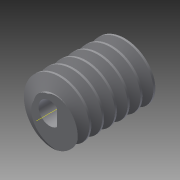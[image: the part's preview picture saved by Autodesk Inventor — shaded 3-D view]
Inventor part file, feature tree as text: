
AUTODESK INVENTOR PART (.ipt)
format: ipt  version: 2015 (Build 190159000, 159)  size: 285,696 bytes
history: native  units: mm
features: sketch x5, extrude x5, helix x1, projected_geometry x1
ambient origin geometry x8: Origin, YZ Plane, XZ Plane, XY Plane, X Axis, Y Axis, Z Axis, Center Point
bodies: Solid1 (feature_tree)
feature tree (12):
  helix  "Coil1"  [1 undecoded]
  sketch  "Sketch2"  dims[d5=3.175mm d6=10.0mm d7=100.0mm d8=0.0mm d9=90.0deg d10=90.0deg d11=0.0mm d12=0.0mm d13=5.5mm]
  extrude  "Extrusion1"  Depth=2.54mm
  extrude  "Extrusion2"  Depth=10.0mm
  extrude  "Extrusion3"  Depth=20.0mm
  extrude  "Extrusion4"  Depth=2.0mm TaperAngle=0.0deg
  extrude  "Extrusion5"  Depth=4.0mm TaperAngle=0.0deg
  sketch  "Sketch1"  dims[d3=1.25mm d4=2.54mm]
  sketch  "Sketch3"  dims[d15=22.0mm d16=0.0mm d17=20.0mm]
  sketch  "Sketch4"  dims[d18=20.0mm d19=0.0mm d20=2.0mm d21=0.0mm]
  sketch  "Sketch5"  dims[d22=20.0mm d23=4.0mm d24=0.0mm d25=4.572mm d26=3.0mm d27=0.0mm d28=8.0mm d29=7.3025mm d30=0.5mm]
  projected_geometry  "Projected Loop1"
note: 1 required parameter value undecoded (feature->parameter linkage not recoverable at this tier; creation-order binding heuristic only, values carry confidence <= 0.55)
